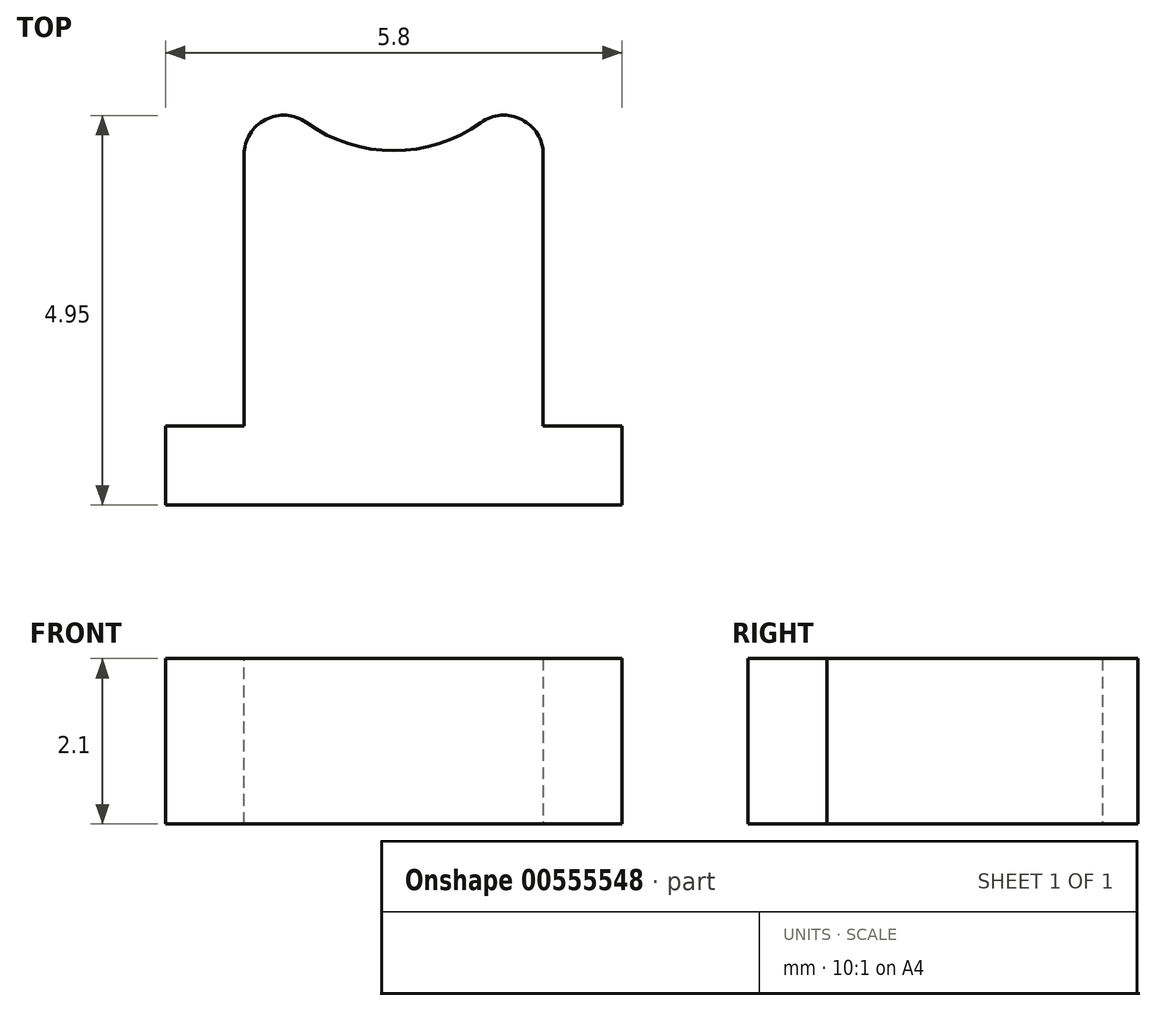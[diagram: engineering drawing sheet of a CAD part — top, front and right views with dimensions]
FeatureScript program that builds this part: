
annotation { "Feature Type Name" : "Feature", "Feature Type Description" : "" }
export const myFeature = defineFeature(function(context is Context, id is Id, definition is map)
    precondition{}
    {
        {
            var Q0;
            Q0=qCreatedBy(makeId("Top.planeOp"),FACE);
            var sketch = newSketch(context, id + "F0", { "sketchPlane" : qUnion([Q0])});
            skLineSegment(sketch, "E0", {"start": v(-3.9, -0.27) * mm, "end": v(1.9, -0.27) * mm});
            skLineSegment(sketch, "E1", {"start": v(1.9, -0.27) * mm, "end": v(1.9, 0.73) * mm});
            skLineSegment(sketch, "E2", {"start": v(1.9, 0.73) * mm, "end": v(0.9, 0.73) * mm});
            skLineSegment(sketch, "E3", {"start": v(0.9, 0.73) * mm, "end": v(0.9, 6.13) * mm});
            skLineSegment(sketch, "E4", {"start": v(-2.9, 6.13) * mm, "end": v(-2.9, 0.73) * mm});
            skLineSegment(sketch, "E5", {"start": v(-2.9, 0.73) * mm, "end": v(-3.9, 0.73) * mm});
            skLineSegment(sketch, "E6", {"start": v(-3.9, 0.73) * mm, "end": v(-3.9, -0.27) * mm});
            skLineSegment(sketch, "E7", {"start": v(-2.9, 6.13) * mm, "end": v(0.9, 6.13) * mm});
            skCircle(sketch, "E8", {"center": v(-1, 6.13) * mm, "radius": 1.9 * mm});
            skLineSegment(sketch, "E9", {"start": v(-2.9, 4.23) * mm, "end": v(0.9, 4.23) * mm, "construction": true});
            skSolve(sketch);
        }
        {
            var Q0;
            Q0=makeQuery(id+"F0.imprint","IMPRINT",FACE,{"disambiguationData":[TD([[makeQuery(id+"F0.imprint","IMPRINT",EDGE,{"derivedFrom":sQuery(id+"F0.wireOp",EDGE,"E0")}),1.0]])]});
            extrude(context, id + "F1", {"entities" : qUnion([Q0]), "depth" : 2.1 * mm, "offsetDistance" : 25 * mm});
        }
        {
            var Q0;
            Q0=makeQuery(id+"F1.opExtrude","SWEPT_EDGE",EDGE,{"disambiguationData":[OSD([sQuery(id+"F0.wireOp",EDGE,"E4"),sQuery(id+"F0.wireOp",EDGE,"E7"),sQuery(id+"F0.wireOp",EDGE,"E8")])]});
            var Q1;
            Q1=makeQuery(id+"F1.opExtrude","SWEPT_EDGE",EDGE,{"disambiguationData":[OSD([sQuery(id+"F0.wireOp",EDGE,"E3"),sQuery(id+"F0.wireOp",EDGE,"E7"),sQuery(id+"F0.wireOp",EDGE,"E8")])]});
            fillet(context, id + "F2", {"entities" : qUnion([Q0, Q1]), "radius" : 0.5 * mm, "tangentPropagation" : true, "allowEdgeOverflow" : false});
        }
    });
